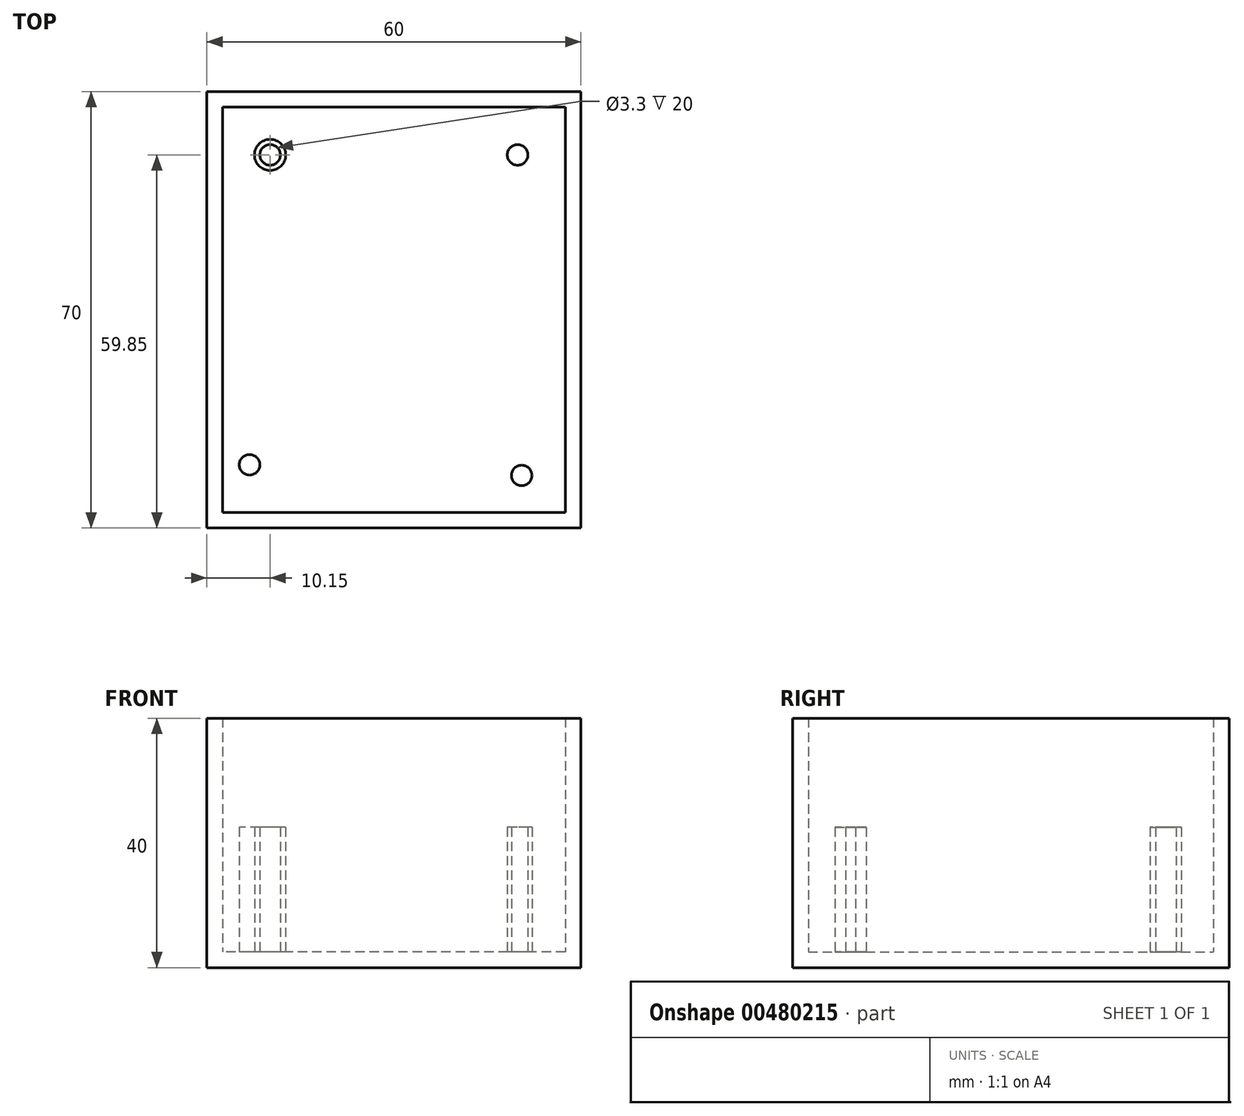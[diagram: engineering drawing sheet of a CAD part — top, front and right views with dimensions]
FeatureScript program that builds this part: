
annotation { "Feature Type Name" : "Feature", "Feature Type Description" : "" }
export const myFeature = defineFeature(function(context is Context, id is Id, definition is map)
    precondition{}
    {
        {
            assignVariable(context, id + "F0", {"name" : "hauteurboite", "anyValue" : 40});
        }
        {
            var Q0;
            Q0=qCreatedBy(makeId("Top.planeOp"),FACE);
            var sketch = newSketch(context, id + "F1", { "sketchPlane" : qUnion([Q0])});
            skLineSegment(sketch, "E0.bottom", {"start": v(30, -35) * mm, "end": v(-30, -35) * mm});
            skLineSegment(sketch, "E0.top", {"start": v(30, 35) * mm, "end": v(-30, 35) * mm});
            skLineSegment(sketch, "E0.left", {"start": v(30, -35) * mm, "end": v(30, 35) * mm});
            skLineSegment(sketch, "E0.right", {"start": v(-30, -35) * mm, "end": v(-30, 35) * mm});
            skPoint(sketch, "E0.middle", {"position": v(0, 0) * mm});
            skSolve(sketch);
        }
        {
            var Q0;
            Q0 = qSketchRegion(id + "F1", true);
            extrude(context, id + "F2", {"entities" : qUnion([Q0]), "depth" : (getVariable(context, 'hauteurboite')) * mm});
        }
        {
            var Q0;
            Q0=makeQuery(id+"F2.opExtrude","CAP_FACE",FACE,{"disambiguationData":[OSD([sQuery(id+"F1.wireOp",EDGE,"E0.bottom"),sQuery(id+"F1.wireOp",EDGE,"E0.top"),sQuery(id+"F1.wireOp",EDGE,"E0.left"),sQuery(id+"F1.wireOp",EDGE,"E0.right")])],"isStart":false});
            shell(context, id + "F3", {"entities" : qUnion([Q0]), "thickness" : 2.5 * mm});
        }
        {
            var Q0;
            Q0=makeQuery(id+"F3.opShell","OFFSET_FACE",FACE,{"disambiguationData":[OSD([sQuery(id+"F1.wireOp",EDGE,"E0.bottom"),sQuery(id+"F1.wireOp",EDGE,"E0.top"),sQuery(id+"F1.wireOp",EDGE,"E0.left"),sQuery(id+"F1.wireOp",EDGE,"E0.right")])]});
            var sketch = newSketch(context, id + "F4", { "sketchPlane" : qUnion([Q0])});
            skCircle(sketch, "E1", {"center": v(-19.85, 24.85) * mm, "radius": 1.65 * mm});
            skCircle(sketch, "E2", {"center": v(-23.15, -24.85) * mm, "radius": 1.65 * mm});
            skCircle(sketch, "E3.MirrorC", {"center": v(19.85, 24.85) * mm, "radius": 1.65 * mm});
            skCircle(sketch, "E4", {"center": v(20.5, -26.56) * mm, "radius": 1.65 * mm});
            skCircle(sketch, "E5", {"center": v(-19.85, 24.85) * mm, "radius": 2.5 * mm});
            skSolve(sketch);
        }
        {
            var Q0;
            Q0 = qSketchRegion(id + "F4", true);
            extrude(context, id + "F5", {"entities" : qUnion([Q0]), "operationType" : NewBodyOperationType.ADD, "depth" : 20 * mm});
        }
    });
